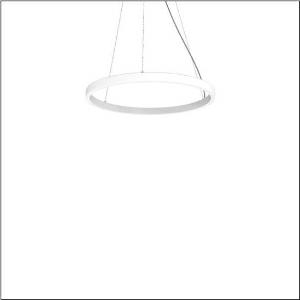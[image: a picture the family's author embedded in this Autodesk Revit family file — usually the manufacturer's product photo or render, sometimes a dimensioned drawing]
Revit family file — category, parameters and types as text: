
# Revit family: silica_r__21_ring-o_5pjbo2d3004a_f563
name_source: partatom
category: Lighting Fixtures
units: mm (PartAtom-declared; Revit-internal decimal feet)

## family parameters
Cut with Voids When Loaded = No
Host = Face
Light Source = No
Part Type = Normal
Room Calculation Point = No
Round Connector Dimension = Use Diameter
Shared = No

## types (1)
- Silica® 21 Ring-O (1 x LED, 4940 lm, 80 W, 4000K)
    Apparent Load = 80 VA
    CIE Flux Codes = 2 16 49 50 100
    Color Rendering = 80
    Color Temperature = 4000K
    Default Elevation = 1800 mm
    Description = Silica® 21 Ring-O, suspended luminaire, of PMMA, frosted, light emission: outer ring side luminous distribution, primary light characteristic: symmetric, installation type: suspended mounting, LED, rated luminous flux: 4.940lm, luminous efficacy: 62lm/W, light colour: 840, colour temperature: 4000K, control gear: DALI 2, with terminal, 5-pole, mains connection: 230V, AC/DC, 0/50..60Hz, rated input power: 80W, housing, of extruded aluminium section, traffic white (RAL 9016), diameter: 810mm, ceiling canopy, traffic white (RAL 9016), protection rating (lamp compartment): IP40, insulation class (complete): insulation class I (protective earthing), certification: CE, impact resistance: IK02, permissible operating ambient temperature: 0..+35°C, packaging unit: 1 piece
    Height = 48 mm  [stored 0.15748 ft]
    Lamp = 1 x LED
    Lamp Light Flux = 4940 lm
    Lamp Power = 80 W
    Lamp count = 1
    Length = 810 mm
    Luminous efficacy = 62 lm/W
    Manufacturer = Siteco
    ModVariant = No
    Model = 5PJBO2D3004A
    Mounting Place = Ceiling
    Mounting Type = Pendant
    Number of Poles = 1
    OnlyDefault = Yes
    Power Factor = 1
    Product Name = Silica® 21 Ring-O
    Product group = suspended luminaire
    ProductGroupID = 905
    Protection Class = Protection class I
    Protection Degree = IP 40
    RLX_Detail_Level = 1
    RLX_Emergency_Light_Flux = 0 lm
    RLX_Emergency_Type = 0
    RLX_Emergency_Type_DB = No
    RlxData = <blob elided: 12013 chars, md5=5c6edbb5>
    Socket = socket
    Standby Power = 0 W
    System Light Flux = 4940 lm
    System Power = 80 W
    Type Comments = Product without accessories
    Type Image = l_1258383.jpg
    URL = http://relux.com
    VarID = ---
    Voltage = 0 V
    Weight = 0.00 kg
    Width = 0 mm  [stored 0 ft]

note: [stored X ft] marks values corroborated as IEEE doubles in the binary element streams (Revit-internal decimal feet)

## geometry (parser evidence)
native form markers: Sweep x14
no freeform markers — native parametric forms only
